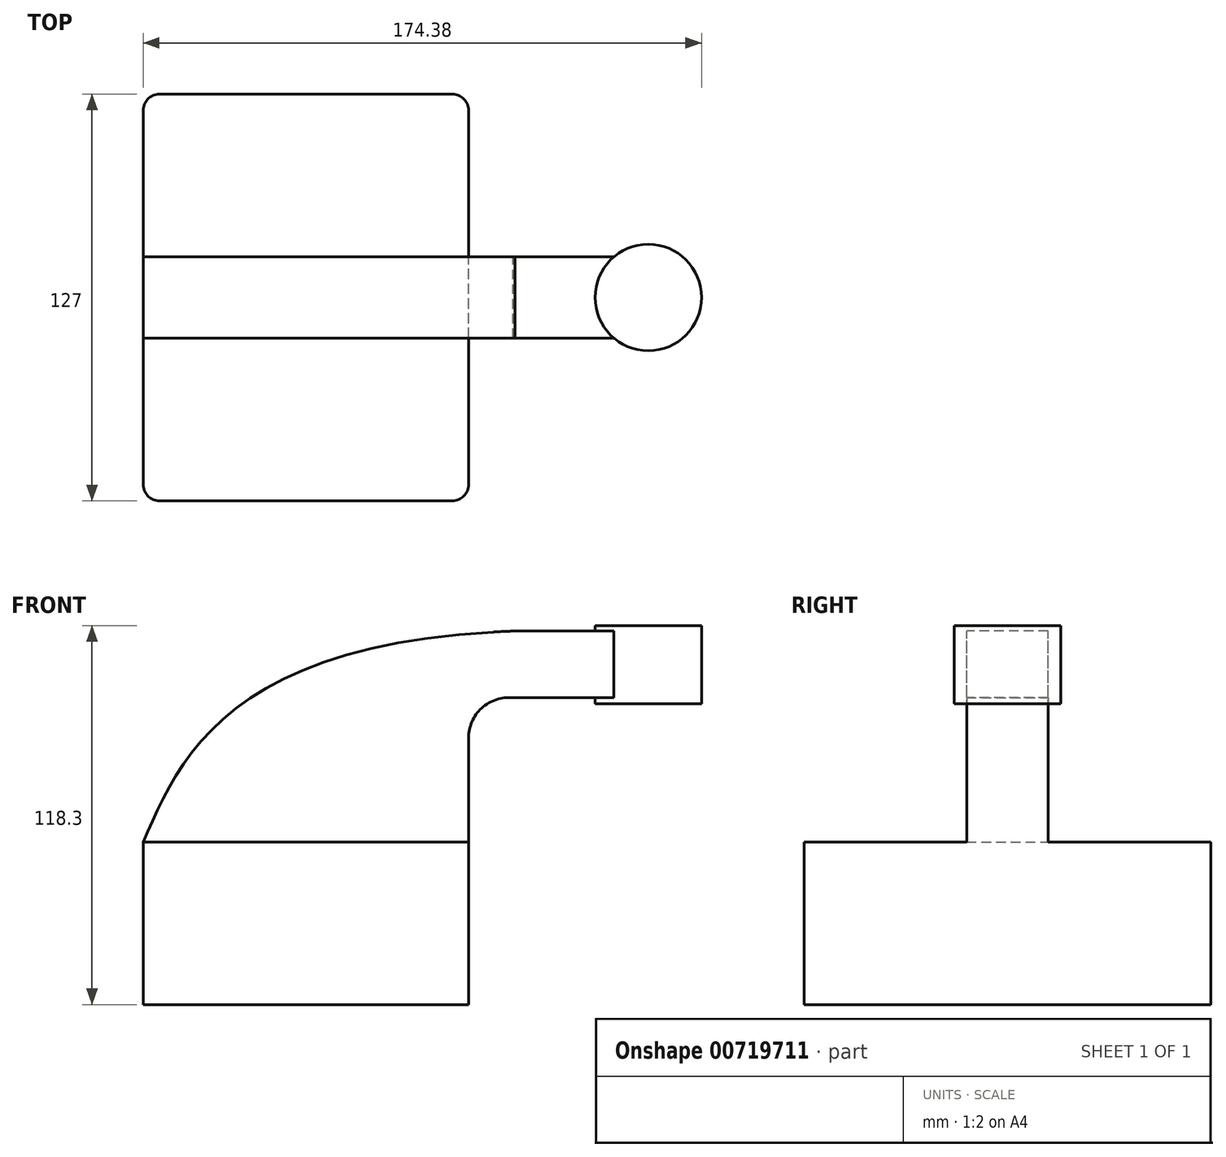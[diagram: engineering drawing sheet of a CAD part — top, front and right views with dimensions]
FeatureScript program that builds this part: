
annotation { "Feature Type Name" : "Feature", "Feature Type Description" : "" }
export const myFeature = defineFeature(function(context is Context, id is Id, definition is map)
    precondition{}
    {
        {
            var Q0;
            Q0=qCreatedBy(makeId("Front.planeOp"),FACE);
            var sketch = newSketch(context, id + "F0", { "sketchPlane" : qUnion([Q0])});
            skLineSegment(sketch, "E0.bottom", {"start": v(-50.8, -25.4) * mm, "end": v(50.8, -25.4) * mm});
            skLineSegment(sketch, "E0.top", {"start": v(-50.8, 25.4) * mm, "end": v(50.8, 25.4) * mm});
            skLineSegment(sketch, "E0.left", {"start": v(-50.8, -25.4) * mm, "end": v(-50.8, 25.4) * mm});
            skLineSegment(sketch, "E0.right", {"start": v(50.8, -25.4) * mm, "end": v(50.8, 25.4) * mm});
            skPoint(sketch, "E0.middle", {"position": v(0, 0) * mm});
            skLineSegment(sketch, "E1.bottom", {"start": v(123.58, 68.57) * mm, "end": v(89.39, 68.57) * mm});
            skLineSegment(sketch, "E1.top", {"start": v(123.58, 92.9) * mm, "end": v(89.39, 92.9) * mm});
            skLineSegment(sketch, "E1.left", {"start": v(123.58, 68.57) * mm, "end": v(123.58, 92.9) * mm});
            skLineSegment(sketch, "E1.right", {"start": v(89.39, 68.57) * mm, "end": v(89.39, 92.9) * mm});
            skPoint(sketch, "E1.middle", {"position": v(106.49, 80.73) * mm});
            skLineSegment(sketch, "E2", {"start": v(50.8, 25.4) * mm, "end": v(50.8, 57.79) * mm});
            skArc(sketch, "E3", {"start": v(50.8, 57.79) * mm, "mid": v(54.93, 67.16) * mm, "end": v(64.62, 70.44) * mm});
            skLineSegment(sketch, "E4", {"start": v(64.62, 70.44) * mm, "end": v(106.96, 70.44) * mm});
            skLineSegment(sketch, "E5.0", {"start": v(65.32, 91.26) * mm, "end": v(106.96, 91.26) * mm});
            skArc(sketch, "E5.1", {"start": v(29.97, 57.79) * mm, "mid": v(40.45, 82.13) * mm, "end": v(65.32, 91.26) * mm});
            skLineSegment(sketch, "E5.2", {"start": v(29.97, 25.4) * mm, "end": v(29.97, 57.79) * mm});
            skLineSegment(sketch, "E6", {"start": v(106.96, 92.9) * mm, "end": v(106.96, 68.57) * mm});
            skFitSpline(sketch, "E7", {"points": [v(-50.8, 25.4) * mm, v(65.32, 91.26) * mm], "startDerivative": vector(33.07, 74.57) * mm, "endDerivative": vector(272.2, 9.86) * mm});
            skSolve(sketch);
        }
        {
            var Q0;
            Q0=makeQuery(id+"F0.imprint","IMPRINT",FACE,{"disambiguationData":[TD([[makeQuery(id+"F0.imprint","IMPRINT",EDGE,{"derivedFrom":sQuery(id+"F0.wireOp",EDGE,"E0.bottom")}),1.0]])]});
            extrude(context, id + "F1", {"entities" : qUnion([Q0]), "endBound" : BoundingType.SYMMETRIC, "depth" : 127 * mm, "offsetDistance" : 25.4 * mm});
        }
        {
            var Q0;
            {var subQ3=sQuery(id+"F0.wireOp",EDGE,"E5.2");Q0=makeQuery(id+"F0.imprint","IMPRINT",FACE,{"disambiguationData":[TD([[makeQuery(id+"F0.imprint","IMPRINT",EDGE,{"derivedFrom":subQ3}),1.0]])]});}
            var Q1;
            {var subQ1=sQuery(id+"F0.wireOp",EDGE,"E2");Q1=makeQuery(id+"F0.imprint","IMPRINT",FACE,{"disambiguationData":[TD([[makeQuery(id+"F0.imprint","IMPRINT",EDGE,{"derivedFrom":subQ1}),1.0]])]});}
            var Q2;
            {var subQ0=sQuery(id+"F0.wireOp",EDGE,"E4");var subQ1=sQuery(id+"F0.wireOp",EDGE,"E1.right");var subQ2=makeQuery(id+"F0.imprint","INTERSECT",VERTEX,{"derivedFrom":[subQ1,subQ0]});Q2=makeQuery(id+"F0.imprint","IMPRINT",FACE,{"disambiguationData":[TD([[makeQuery(id+"F0.imprint","IMPRINT",EDGE,{"disambiguationData":[TD([[subQ2,-1.0]])],"derivedFrom":subQ1}),-1.0]])]});}
            extrude(context, id + "F2", {"entities" : qUnion([Q0, Q1, Q2]), "operationType" : NewBodyOperationType.ADD, "endBound" : BoundingType.SYMMETRIC, "depth" : 25.4 * mm, "offsetDistance" : 25.4 * mm});
        }
        {
            var Q0;
            {var subQ0=sQuery(id+"F0.wireOp",EDGE,"E1.left");Q0=makeQuery(id+"F0.imprint","IMPRINT",FACE,{"disambiguationData":[TD([[makeQuery(id+"F0.imprint","IMPRINT",EDGE,{"derivedFrom":subQ0}),1.0]])]});}
            var Q1;
            Q1=sQuery(id+"F0.wireOp",EDGE,"E6");
            revolve(context, id + "F3", {"operationType" : NewBodyOperationType.ADD, "surfaceOperationType" : NewSurfaceOperationType.NEW, "entities" : qUnion([Q0]), "axis" : qUnion([Q1]), "revolveType" : RevolveType.FULL});
        }
        {
            var Q0;
            Q0=makeQuery(id+"F1.opExtrude","CAP_EDGE",EDGE,{"disambiguationData":[OSD([sQuery(id+"F0.wireOp",EDGE,"E0.right")])],"isStart":false});
            var Q1;
            Q1=makeQuery(id+"F1.opExtrude","CAP_EDGE",EDGE,{"disambiguationData":[OSD([sQuery(id+"F0.wireOp",EDGE,"E0.left")])],"isStart":false});
            var Q2;
            Q2=makeQuery(id+"F1.opExtrude","CAP_EDGE",EDGE,{"disambiguationData":[OSD([sQuery(id+"F0.wireOp",EDGE,"E0.right")])],"isStart":true});
            fillet(context, id + "F4", {"entities" : qUnion([Q0, Q1, Q2]), "radius" : 5.08 * mm, "tangentPropagation" : true, "allowEdgeOverflow" : false});
        }
        {
            var Q0;
            Q0=makeQuery(id+"F1.opExtrude","CAP_EDGE",EDGE,{"disambiguationData":[OSD([sQuery(id+"F0.wireOp",EDGE,"E0.left")])],"isStart":true});
            fillet(context, id + "F5", {"entities" : qUnion([Q0]), "radius" : 5.08 * mm, "tangentPropagation" : true, "allowEdgeOverflow" : false});
        }
    });
